# Revit family: BAS-IP_Видеодомофон_AT-07L
name_source: partatom
category: Устройства связи
units: mm (PartAtom-declared; Revit-internal decimal feet)

## family parameters
Всегда вертикально = Да
На основе рабочей плоскости = Нет
Общий = Нет
При загрузке вырезать с полостями = Нет
Размер круглого соединителя = Использовать диаметр
Сохранять ориентацию аннотаций = Нет
Тип детали = Нормальный
Точка расчета площади = Нет

## types (2) — shared parameters
ADSK_Единица измерения = шт.
ADSK_Завод-изготовитель = BAS-IP
ADSK_Количество = 1
ADSK_Наименование = IP видеодомофон
Встроенная камера = Нет
Габаритные размеры = 236 x 128 x 26,5 мм
Дисплей = 7” IPS LCD, сенсорный емкостный
Изготовитель = BAS-IP
Корпус = Алюминий
Питание = PoE, +12 В
Потребление питания = 6 Вт, в режиме ожидания - 2,5 Вт
Разрешение экрана = 1024 x 600
Тип установки = Настенный накладной, врезной (кронштейны в комплекте)

## per-type parameters (varying)
| type | ADSK_Марка | ADSK_Материал | Цвет | Цвет логотипа |
| Белый | AT-07L White | Silver | White | Black |
| Черный | AT-07L Black | Black silver | Black silver 2 | White |

note: column(s) folded — value = type name in every type: Цветовое решение
